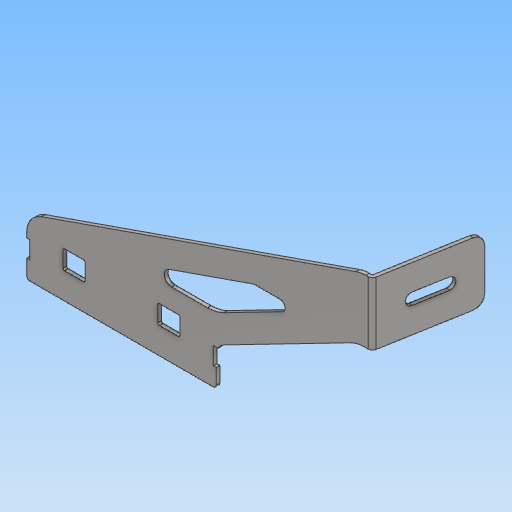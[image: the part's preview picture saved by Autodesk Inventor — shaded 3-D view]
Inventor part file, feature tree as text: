
AUTODESK INVENTOR PART (.ipt)
format: ipt  version: 2020 (Build 240168000, 168)  size: 431,616 bytes
history: native  units: mm
features: other x3, extrude x1, plane x1
ambient origin geometry x8: Origin, YZ Plane, XZ Plane, XY Plane, X Axis, Y Axis, Z Axis, Center Point
bodies: Body1 (feature_tree)
feature tree (5):
  other  "實體1"
  extrude  "擠出1"  Depth=130.0mm
  other  "折彎零件1"
  plane  "工作平面1"
  other  "定義1"
